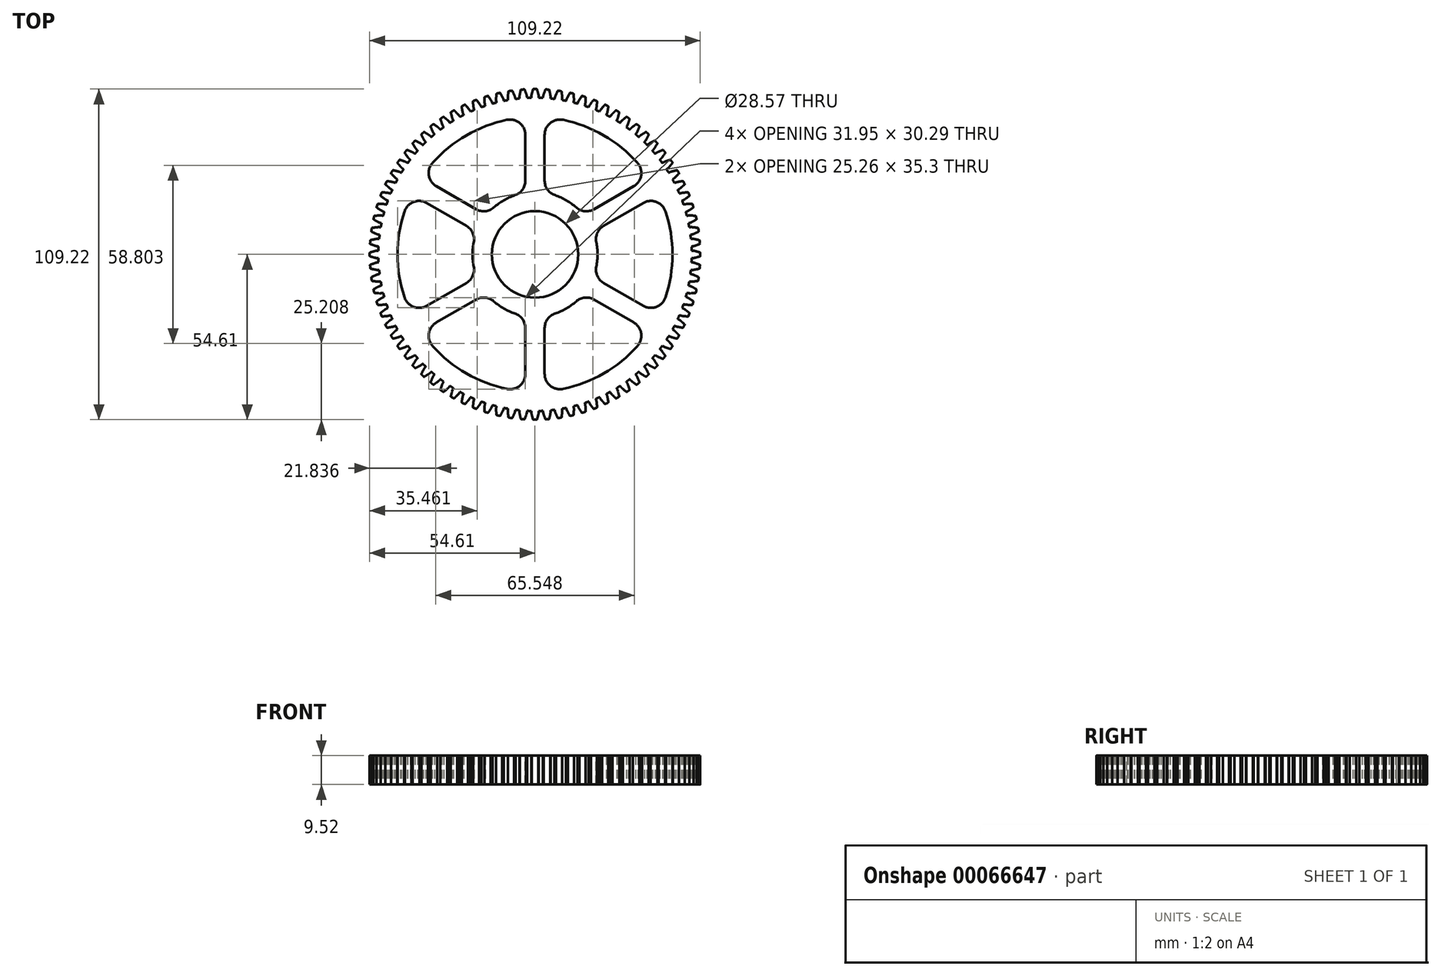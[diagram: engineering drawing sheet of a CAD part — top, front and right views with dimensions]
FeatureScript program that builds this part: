
annotation { "Feature Type Name" : "Feature", "Feature Type Description" : "" }
export const myFeature = defineFeature(function(context is Context, id is Id, definition is map)
    precondition{}
    {
        {
            var Q0;
            Q0=qCreatedBy(makeId("Top.planeOp"),FACE);
            var sketch = newSketch(context, id + "F0", { "sketchPlane" : qUnion([Q0])});
            skArc(sketch, "E0", {"start": v(1.25, 51.74) * mm, "mid": v(0, 51.75) * mm, "end": v(-1.25, 51.74) * mm});
            skArc(sketch, "E1", {"start": v(-1.25, -51.74) * mm, "mid": v(51.74, -1.25) * mm, "end": v(1.25, 51.74) * mm});
            skArc(sketch, "E2", {"start": v(-1.05, 53.12) * mm, "mid": v(-1.2, 52.43) * mm, "end": v(-1.25, 51.74) * mm});
            skArc(sketch, "E3", {"start": v(-0.67, 54.46) * mm, "mid": v(-0.86, 53.79) * mm, "end": v(-1.05, 53.12) * mm});
            skArc(sketch, "E4", {"start": v(-0.48, 54.6) * mm, "mid": v(-0.6, 54.57) * mm, "end": v(-0.67, 54.46) * mm});
            skArc(sketch, "E5", {"start": v(1.25, 51.74) * mm, "mid": v(1.2, 52.43) * mm, "end": v(1.05, 53.12) * mm});
            skArc(sketch, "E6", {"start": v(1.05, 53.12) * mm, "mid": v(0.86, 53.79) * mm, "end": v(0.67, 54.46) * mm});
            skArc(sketch, "E7", {"start": v(0.48, 54.6) * mm, "mid": v(0, 54.61) * mm, "end": v(-0.48, 54.6) * mm});
            skArc(sketch, "E8", {"start": v(0.67, 54.46) * mm, "mid": v(0.6, 54.57) * mm, "end": v(0.48, 54.6) * mm});
            skArc(sketch, "E9", {"start": v(-1.25, 51.74) * mm, "mid": v(-51.75, 0) * mm, "end": v(-1.25, -51.74) * mm});
            skSolve(sketch);
        }
        {
            var Q0;
            Q0=makeQuery(id+"F0.imprint","IMPRINT",FACE,{"disambiguationData":[TD([[makeQuery(id+"F0.imprint","IMPRINT",EDGE,{"derivedFrom":sQuery(id+"F0.wireOp",EDGE,"E0")}),1.0]])]});
            extrude(context, id + "F1", {"entities" : qUnion([Q0]), "endBound" : BoundingType.SYMMETRIC, "depth" : 9.52 * mm});
        }
        {
            var Q0;
            {var subQ0=sQuery(id+"F0.wireOp",EDGE,"E0");Q0=makeQuery(id+"F0.imprint","IMPRINT",FACE,{"disambiguationData":[TD([[makeQuery(id+"F0.imprint","IMPRINT",EDGE,{"derivedFrom":subQ0}),-1.0]])]});}
            var Q1;
            Q1=makeQuery(id+"F1.opExtrude","CAP_FACE",FACE,{"disambiguationData":[OSD([sQuery(id+"F0.wireOp",EDGE,"E0"),sQuery(id+"F0.wireOp",EDGE,"E1"),sQuery(id+"F0.wireOp",EDGE,"E9")])],"isStart":false});
            var Q2;
            Q2=makeQuery(id+"F1.opExtrude","CAP_FACE",FACE,{"disambiguationData":[OSD([sQuery(id+"F0.wireOp",EDGE,"E0"),sQuery(id+"F0.wireOp",EDGE,"E1"),sQuery(id+"F0.wireOp",EDGE,"E9")])],"isStart":true});
            extrude(context, id + "F2", {"entities" : qUnion([Q0]), "endBound" : BoundingType.UP_TO_SURFACE, "endBoundEntityFace" : qUnion([Q1]), "depth" : 25.4 * mm, "hasSecondDirection" : true, "secondDirectionBound" : SecondDirectionBoundingType.UP_TO_SURFACE, "secondDirectionOppositeDirection" : true, "secondDirectionBoundEntityFace" : qUnion([Q2]), "secondDirectionDepth" : 25.4 * mm});
        }
        {
            var Q0;
            Q0=makeQuery(id+"F2.opExtrude","SWEPT_BODY",BODY,{"disambiguationData":[OSD([sQuery(id+"F0.wireOp",EDGE,"E0"),sQuery(id+"F0.wireOp",EDGE,"E2"),sQuery(id+"F0.wireOp",EDGE,"E3"),sQuery(id+"F0.wireOp",EDGE,"E4"),sQuery(id+"F0.wireOp",EDGE,"E5"),sQuery(id+"F0.wireOp",EDGE,"E6"),sQuery(id+"F0.wireOp",EDGE,"E7"),sQuery(id+"F0.wireOp",EDGE,"E8")])]});
            var Q1;
            Q1=makeQuery(id+"F1.opExtrude","SWEPT_FACE",FACE,{"disambiguationData":[OSD([sQuery(id+"F0.wireOp",EDGE,"E0"),sQuery(id+"F0.wireOp",EDGE,"E1"),sQuery(id+"F0.wireOp",EDGE,"E9")])]});
            circularPattern(context, id + "F3", {"operationType" : NewBodyOperationType.ADD, "entities" : qUnion([Q0]), "axis" : qUnion([Q1]), "angle" : 360 * degree, "instanceCount" : 84, "equalSpace" : true});
        }
        {
            var Q0;
            {var subQ0=sQuery(id+"F0.wireOp",EDGE,"E0");var subQ1=makeQuery(id+"F2.opExtrude","CAP_FACE",FACE,{"disambiguationData":[OSD([subQ0,sQuery(id+"F0.wireOp",EDGE,"E2"),sQuery(id+"F0.wireOp",EDGE,"E3"),sQuery(id+"F0.wireOp",EDGE,"E4"),sQuery(id+"F0.wireOp",EDGE,"E5"),sQuery(id+"F0.wireOp",EDGE,"E6"),sQuery(id+"F0.wireOp",EDGE,"E7"),sQuery(id+"F0.wireOp",EDGE,"E8")])],"isStart":false});Q0=makeQuery(id+"F3.boolean.opBoolean","MERGE",FACE,{"derivedFrom":[makeQuery(id+"F1.opExtrude","CAP_FACE",FACE,{"disambiguationData":[OSD([subQ0,sQuery(id+"F0.wireOp",EDGE,"E1"),sQuery(id+"F0.wireOp",EDGE,"E9")])],"isStart":false}),subQ1,makeQuery(id+"F3.opPattern","COPY",FACE,{"derivedFrom":subQ1,"instanceName":"1"}),makeQuery(id+"F3.opPattern","COPY",FACE,{"derivedFrom":subQ1,"instanceName":"2"}),makeQuery(id+"F3.opPattern","COPY",FACE,{"derivedFrom":subQ1,"instanceName":"3"}),makeQuery(id+"F3.opPattern","COPY",FACE,{"derivedFrom":subQ1,"instanceName":"4"}),makeQuery(id+"F3.opPattern","COPY",FACE,{"derivedFrom":subQ1,"instanceName":"5"}),makeQuery(id+"F3.opPattern","COPY",FACE,{"derivedFrom":subQ1,"instanceName":"6"}),makeQuery(id+"F3.opPattern","COPY",FACE,{"derivedFrom":subQ1,"instanceName":"7"}),makeQuery(id+"F3.opPattern","COPY",FACE,{"derivedFrom":subQ1,"instanceName":"8"}),makeQuery(id+"F3.opPattern","COPY",FACE,{"derivedFrom":subQ1,"instanceName":"9"}),makeQuery(id+"F3.opPattern","COPY",FACE,{"derivedFrom":subQ1,"instanceName":"10"}),makeQuery(id+"F3.opPattern","COPY",FACE,{"derivedFrom":subQ1,"instanceName":"11"}),makeQuery(id+"F3.opPattern","COPY",FACE,{"derivedFrom":subQ1,"instanceName":"12"}),makeQuery(id+"F3.opPattern","COPY",FACE,{"derivedFrom":subQ1,"instanceName":"13"}),makeQuery(id+"F3.opPattern","COPY",FACE,{"derivedFrom":subQ1,"instanceName":"14"}),makeQuery(id+"F3.opPattern","COPY",FACE,{"derivedFrom":subQ1,"instanceName":"15"}),makeQuery(id+"F3.opPattern","COPY",FACE,{"derivedFrom":subQ1,"instanceName":"16"}),makeQuery(id+"F3.opPattern","COPY",FACE,{"derivedFrom":subQ1,"instanceName":"17"}),makeQuery(id+"F3.opPattern","COPY",FACE,{"derivedFrom":subQ1,"instanceName":"18"}),makeQuery(id+"F3.opPattern","COPY",FACE,{"derivedFrom":subQ1,"instanceName":"19"}),makeQuery(id+"F3.opPattern","COPY",FACE,{"derivedFrom":subQ1,"instanceName":"20"}),makeQuery(id+"F3.opPattern","COPY",FACE,{"derivedFrom":subQ1,"instanceName":"21"}),makeQuery(id+"F3.opPattern","COPY",FACE,{"derivedFrom":subQ1,"instanceName":"22"}),makeQuery(id+"F3.opPattern","COPY",FACE,{"derivedFrom":subQ1,"instanceName":"23"}),makeQuery(id+"F3.opPattern","COPY",FACE,{"derivedFrom":subQ1,"instanceName":"24"}),makeQuery(id+"F3.opPattern","COPY",FACE,{"derivedFrom":subQ1,"instanceName":"25"}),makeQuery(id+"F3.opPattern","COPY",FACE,{"derivedFrom":subQ1,"instanceName":"26"}),makeQuery(id+"F3.opPattern","COPY",FACE,{"derivedFrom":subQ1,"instanceName":"27"}),makeQuery(id+"F3.opPattern","COPY",FACE,{"derivedFrom":subQ1,"instanceName":"28"}),makeQuery(id+"F3.opPattern","COPY",FACE,{"derivedFrom":subQ1,"instanceName":"29"}),makeQuery(id+"F3.opPattern","COPY",FACE,{"derivedFrom":subQ1,"instanceName":"30"}),makeQuery(id+"F3.opPattern","COPY",FACE,{"derivedFrom":subQ1,"instanceName":"31"}),makeQuery(id+"F3.opPattern","COPY",FACE,{"derivedFrom":subQ1,"instanceName":"32"}),makeQuery(id+"F3.opPattern","COPY",FACE,{"derivedFrom":subQ1,"instanceName":"33"}),makeQuery(id+"F3.opPattern","COPY",FACE,{"derivedFrom":subQ1,"instanceName":"34"}),makeQuery(id+"F3.opPattern","COPY",FACE,{"derivedFrom":subQ1,"instanceName":"35"}),makeQuery(id+"F3.opPattern","COPY",FACE,{"derivedFrom":subQ1,"instanceName":"36"}),makeQuery(id+"F3.opPattern","COPY",FACE,{"derivedFrom":subQ1,"instanceName":"37"}),makeQuery(id+"F3.opPattern","COPY",FACE,{"derivedFrom":subQ1,"instanceName":"38"}),makeQuery(id+"F3.opPattern","COPY",FACE,{"derivedFrom":subQ1,"instanceName":"39"}),makeQuery(id+"F3.opPattern","COPY",FACE,{"derivedFrom":subQ1,"instanceName":"40"}),makeQuery(id+"F3.opPattern","COPY",FACE,{"derivedFrom":subQ1,"instanceName":"41"}),makeQuery(id+"F3.opPattern","COPY",FACE,{"derivedFrom":subQ1,"instanceName":"42"}),makeQuery(id+"F3.opPattern","COPY",FACE,{"derivedFrom":subQ1,"instanceName":"43"}),makeQuery(id+"F3.opPattern","COPY",FACE,{"derivedFrom":subQ1,"instanceName":"44"}),makeQuery(id+"F3.opPattern","COPY",FACE,{"derivedFrom":subQ1,"instanceName":"45"}),makeQuery(id+"F3.opPattern","COPY",FACE,{"derivedFrom":subQ1,"instanceName":"46"}),makeQuery(id+"F3.opPattern","COPY",FACE,{"derivedFrom":subQ1,"instanceName":"47"}),makeQuery(id+"F3.opPattern","COPY",FACE,{"derivedFrom":subQ1,"instanceName":"48"}),makeQuery(id+"F3.opPattern","COPY",FACE,{"derivedFrom":subQ1,"instanceName":"49"}),makeQuery(id+"F3.opPattern","COPY",FACE,{"derivedFrom":subQ1,"instanceName":"50"}),makeQuery(id+"F3.opPattern","COPY",FACE,{"derivedFrom":subQ1,"instanceName":"51"}),makeQuery(id+"F3.opPattern","COPY",FACE,{"derivedFrom":subQ1,"instanceName":"52"}),makeQuery(id+"F3.opPattern","COPY",FACE,{"derivedFrom":subQ1,"instanceName":"53"}),makeQuery(id+"F3.opPattern","COPY",FACE,{"derivedFrom":subQ1,"instanceName":"54"}),makeQuery(id+"F3.opPattern","COPY",FACE,{"derivedFrom":subQ1,"instanceName":"55"}),makeQuery(id+"F3.opPattern","COPY",FACE,{"derivedFrom":subQ1,"instanceName":"56"}),makeQuery(id+"F3.opPattern","COPY",FACE,{"derivedFrom":subQ1,"instanceName":"57"}),makeQuery(id+"F3.opPattern","COPY",FACE,{"derivedFrom":subQ1,"instanceName":"58"}),makeQuery(id+"F3.opPattern","COPY",FACE,{"derivedFrom":subQ1,"instanceName":"59"}),makeQuery(id+"F3.opPattern","COPY",FACE,{"derivedFrom":subQ1,"instanceName":"60"}),makeQuery(id+"F3.opPattern","COPY",FACE,{"derivedFrom":subQ1,"instanceName":"61"}),makeQuery(id+"F3.opPattern","COPY",FACE,{"derivedFrom":subQ1,"instanceName":"62"}),makeQuery(id+"F3.opPattern","COPY",FACE,{"derivedFrom":subQ1,"instanceName":"63"}),makeQuery(id+"F3.opPattern","COPY",FACE,{"derivedFrom":subQ1,"instanceName":"64"}),makeQuery(id+"F3.opPattern","COPY",FACE,{"derivedFrom":subQ1,"instanceName":"65"}),makeQuery(id+"F3.opPattern","COPY",FACE,{"derivedFrom":subQ1,"instanceName":"66"}),makeQuery(id+"F3.opPattern","COPY",FACE,{"derivedFrom":subQ1,"instanceName":"67"}),makeQuery(id+"F3.opPattern","COPY",FACE,{"derivedFrom":subQ1,"instanceName":"68"}),makeQuery(id+"F3.opPattern","COPY",FACE,{"derivedFrom":subQ1,"instanceName":"69"}),makeQuery(id+"F3.opPattern","COPY",FACE,{"derivedFrom":subQ1,"instanceName":"70"}),makeQuery(id+"F3.opPattern","COPY",FACE,{"derivedFrom":subQ1,"instanceName":"71"}),makeQuery(id+"F3.opPattern","COPY",FACE,{"derivedFrom":subQ1,"instanceName":"72"}),makeQuery(id+"F3.opPattern","COPY",FACE,{"derivedFrom":subQ1,"instanceName":"73"}),makeQuery(id+"F3.opPattern","COPY",FACE,{"derivedFrom":subQ1,"instanceName":"74"}),makeQuery(id+"F3.opPattern","COPY",FACE,{"derivedFrom":subQ1,"instanceName":"75"}),makeQuery(id+"F3.opPattern","COPY",FACE,{"derivedFrom":subQ1,"instanceName":"76"}),makeQuery(id+"F3.opPattern","COPY",FACE,{"derivedFrom":subQ1,"instanceName":"77"}),makeQuery(id+"F3.opPattern","COPY",FACE,{"derivedFrom":subQ1,"instanceName":"78"}),makeQuery(id+"F3.opPattern","COPY",FACE,{"derivedFrom":subQ1,"instanceName":"79"}),makeQuery(id+"F3.opPattern","COPY",FACE,{"derivedFrom":subQ1,"instanceName":"80"}),makeQuery(id+"F3.opPattern","COPY",FACE,{"derivedFrom":subQ1,"instanceName":"81"}),makeQuery(id+"F3.opPattern","COPY",FACE,{"derivedFrom":subQ1,"instanceName":"82"}),makeQuery(id+"F3.opPattern","COPY",FACE,{"derivedFrom":subQ1,"instanceName":"83"})]});}
            var sketch = newSketch(context, id + "F4", { "sketchPlane" : qUnion([Q0])});
            skCircle(sketch, "E10", {"center": v(0, 0) * mm, "radius": 14.29 * mm});
            skSolve(sketch);
        }
        {
            var Q0;
            Q0=makeQuery(id+"F4.imprint","IMPRINT",FACE,{"disambiguationData":[TD([[makeQuery(id+"F4.imprint","IMPRINT",EDGE,{"derivedFrom":sQuery(id+"F4.wireOp",EDGE,"E10")}),1.0]])]});
            extrude(context, id + "F5", {"entities" : qUnion([Q0]), "operationType" : NewBodyOperationType.REMOVE, "endBound" : BoundingType.UP_TO_NEXT, "oppositeDirection" : true, "depth" : 25.4 * mm});
        }
        {
            var Q0;
            {var subQ0=sQuery(id+"F0.wireOp",EDGE,"E0");var subQ1=makeQuery(id+"F2.opExtrude","CAP_FACE",FACE,{"disambiguationData":[OSD([subQ0,sQuery(id+"F0.wireOp",EDGE,"E2"),sQuery(id+"F0.wireOp",EDGE,"E3"),sQuery(id+"F0.wireOp",EDGE,"E4"),sQuery(id+"F0.wireOp",EDGE,"E5"),sQuery(id+"F0.wireOp",EDGE,"E6"),sQuery(id+"F0.wireOp",EDGE,"E7"),sQuery(id+"F0.wireOp",EDGE,"E8")])],"isStart":false});Q0=makeQuery(id+"F3.boolean.opBoolean","MERGE",FACE,{"derivedFrom":[makeQuery(id+"F1.opExtrude","CAP_FACE",FACE,{"disambiguationData":[OSD([subQ0,sQuery(id+"F0.wireOp",EDGE,"E1"),sQuery(id+"F0.wireOp",EDGE,"E9")])],"isStart":false}),subQ1,makeQuery(id+"F3.opPattern","COPY",FACE,{"derivedFrom":subQ1,"instanceName":"1"}),makeQuery(id+"F3.opPattern","COPY",FACE,{"derivedFrom":subQ1,"instanceName":"2"}),makeQuery(id+"F3.opPattern","COPY",FACE,{"derivedFrom":subQ1,"instanceName":"3"}),makeQuery(id+"F3.opPattern","COPY",FACE,{"derivedFrom":subQ1,"instanceName":"4"}),makeQuery(id+"F3.opPattern","COPY",FACE,{"derivedFrom":subQ1,"instanceName":"5"}),makeQuery(id+"F3.opPattern","COPY",FACE,{"derivedFrom":subQ1,"instanceName":"6"}),makeQuery(id+"F3.opPattern","COPY",FACE,{"derivedFrom":subQ1,"instanceName":"7"}),makeQuery(id+"F3.opPattern","COPY",FACE,{"derivedFrom":subQ1,"instanceName":"8"}),makeQuery(id+"F3.opPattern","COPY",FACE,{"derivedFrom":subQ1,"instanceName":"9"}),makeQuery(id+"F3.opPattern","COPY",FACE,{"derivedFrom":subQ1,"instanceName":"10"}),makeQuery(id+"F3.opPattern","COPY",FACE,{"derivedFrom":subQ1,"instanceName":"11"}),makeQuery(id+"F3.opPattern","COPY",FACE,{"derivedFrom":subQ1,"instanceName":"12"}),makeQuery(id+"F3.opPattern","COPY",FACE,{"derivedFrom":subQ1,"instanceName":"13"}),makeQuery(id+"F3.opPattern","COPY",FACE,{"derivedFrom":subQ1,"instanceName":"14"}),makeQuery(id+"F3.opPattern","COPY",FACE,{"derivedFrom":subQ1,"instanceName":"15"}),makeQuery(id+"F3.opPattern","COPY",FACE,{"derivedFrom":subQ1,"instanceName":"16"}),makeQuery(id+"F3.opPattern","COPY",FACE,{"derivedFrom":subQ1,"instanceName":"17"}),makeQuery(id+"F3.opPattern","COPY",FACE,{"derivedFrom":subQ1,"instanceName":"18"}),makeQuery(id+"F3.opPattern","COPY",FACE,{"derivedFrom":subQ1,"instanceName":"19"}),makeQuery(id+"F3.opPattern","COPY",FACE,{"derivedFrom":subQ1,"instanceName":"20"}),makeQuery(id+"F3.opPattern","COPY",FACE,{"derivedFrom":subQ1,"instanceName":"21"}),makeQuery(id+"F3.opPattern","COPY",FACE,{"derivedFrom":subQ1,"instanceName":"22"}),makeQuery(id+"F3.opPattern","COPY",FACE,{"derivedFrom":subQ1,"instanceName":"23"}),makeQuery(id+"F3.opPattern","COPY",FACE,{"derivedFrom":subQ1,"instanceName":"24"}),makeQuery(id+"F3.opPattern","COPY",FACE,{"derivedFrom":subQ1,"instanceName":"25"}),makeQuery(id+"F3.opPattern","COPY",FACE,{"derivedFrom":subQ1,"instanceName":"26"}),makeQuery(id+"F3.opPattern","COPY",FACE,{"derivedFrom":subQ1,"instanceName":"27"}),makeQuery(id+"F3.opPattern","COPY",FACE,{"derivedFrom":subQ1,"instanceName":"28"}),makeQuery(id+"F3.opPattern","COPY",FACE,{"derivedFrom":subQ1,"instanceName":"29"}),makeQuery(id+"F3.opPattern","COPY",FACE,{"derivedFrom":subQ1,"instanceName":"30"}),makeQuery(id+"F3.opPattern","COPY",FACE,{"derivedFrom":subQ1,"instanceName":"31"}),makeQuery(id+"F3.opPattern","COPY",FACE,{"derivedFrom":subQ1,"instanceName":"32"}),makeQuery(id+"F3.opPattern","COPY",FACE,{"derivedFrom":subQ1,"instanceName":"33"}),makeQuery(id+"F3.opPattern","COPY",FACE,{"derivedFrom":subQ1,"instanceName":"34"}),makeQuery(id+"F3.opPattern","COPY",FACE,{"derivedFrom":subQ1,"instanceName":"35"}),makeQuery(id+"F3.opPattern","COPY",FACE,{"derivedFrom":subQ1,"instanceName":"36"}),makeQuery(id+"F3.opPattern","COPY",FACE,{"derivedFrom":subQ1,"instanceName":"37"}),makeQuery(id+"F3.opPattern","COPY",FACE,{"derivedFrom":subQ1,"instanceName":"38"}),makeQuery(id+"F3.opPattern","COPY",FACE,{"derivedFrom":subQ1,"instanceName":"39"}),makeQuery(id+"F3.opPattern","COPY",FACE,{"derivedFrom":subQ1,"instanceName":"40"}),makeQuery(id+"F3.opPattern","COPY",FACE,{"derivedFrom":subQ1,"instanceName":"41"}),makeQuery(id+"F3.opPattern","COPY",FACE,{"derivedFrom":subQ1,"instanceName":"42"}),makeQuery(id+"F3.opPattern","COPY",FACE,{"derivedFrom":subQ1,"instanceName":"43"}),makeQuery(id+"F3.opPattern","COPY",FACE,{"derivedFrom":subQ1,"instanceName":"44"}),makeQuery(id+"F3.opPattern","COPY",FACE,{"derivedFrom":subQ1,"instanceName":"45"}),makeQuery(id+"F3.opPattern","COPY",FACE,{"derivedFrom":subQ1,"instanceName":"46"}),makeQuery(id+"F3.opPattern","COPY",FACE,{"derivedFrom":subQ1,"instanceName":"47"}),makeQuery(id+"F3.opPattern","COPY",FACE,{"derivedFrom":subQ1,"instanceName":"48"}),makeQuery(id+"F3.opPattern","COPY",FACE,{"derivedFrom":subQ1,"instanceName":"49"}),makeQuery(id+"F3.opPattern","COPY",FACE,{"derivedFrom":subQ1,"instanceName":"50"}),makeQuery(id+"F3.opPattern","COPY",FACE,{"derivedFrom":subQ1,"instanceName":"51"}),makeQuery(id+"F3.opPattern","COPY",FACE,{"derivedFrom":subQ1,"instanceName":"52"}),makeQuery(id+"F3.opPattern","COPY",FACE,{"derivedFrom":subQ1,"instanceName":"53"}),makeQuery(id+"F3.opPattern","COPY",FACE,{"derivedFrom":subQ1,"instanceName":"54"}),makeQuery(id+"F3.opPattern","COPY",FACE,{"derivedFrom":subQ1,"instanceName":"55"}),makeQuery(id+"F3.opPattern","COPY",FACE,{"derivedFrom":subQ1,"instanceName":"56"}),makeQuery(id+"F3.opPattern","COPY",FACE,{"derivedFrom":subQ1,"instanceName":"57"}),makeQuery(id+"F3.opPattern","COPY",FACE,{"derivedFrom":subQ1,"instanceName":"58"}),makeQuery(id+"F3.opPattern","COPY",FACE,{"derivedFrom":subQ1,"instanceName":"59"}),makeQuery(id+"F3.opPattern","COPY",FACE,{"derivedFrom":subQ1,"instanceName":"60"}),makeQuery(id+"F3.opPattern","COPY",FACE,{"derivedFrom":subQ1,"instanceName":"61"}),makeQuery(id+"F3.opPattern","COPY",FACE,{"derivedFrom":subQ1,"instanceName":"62"}),makeQuery(id+"F3.opPattern","COPY",FACE,{"derivedFrom":subQ1,"instanceName":"63"}),makeQuery(id+"F3.opPattern","COPY",FACE,{"derivedFrom":subQ1,"instanceName":"64"}),makeQuery(id+"F3.opPattern","COPY",FACE,{"derivedFrom":subQ1,"instanceName":"65"}),makeQuery(id+"F3.opPattern","COPY",FACE,{"derivedFrom":subQ1,"instanceName":"66"}),makeQuery(id+"F3.opPattern","COPY",FACE,{"derivedFrom":subQ1,"instanceName":"67"}),makeQuery(id+"F3.opPattern","COPY",FACE,{"derivedFrom":subQ1,"instanceName":"68"}),makeQuery(id+"F3.opPattern","COPY",FACE,{"derivedFrom":subQ1,"instanceName":"69"}),makeQuery(id+"F3.opPattern","COPY",FACE,{"derivedFrom":subQ1,"instanceName":"70"}),makeQuery(id+"F3.opPattern","COPY",FACE,{"derivedFrom":subQ1,"instanceName":"71"}),makeQuery(id+"F3.opPattern","COPY",FACE,{"derivedFrom":subQ1,"instanceName":"72"}),makeQuery(id+"F3.opPattern","COPY",FACE,{"derivedFrom":subQ1,"instanceName":"73"}),makeQuery(id+"F3.opPattern","COPY",FACE,{"derivedFrom":subQ1,"instanceName":"74"}),makeQuery(id+"F3.opPattern","COPY",FACE,{"derivedFrom":subQ1,"instanceName":"75"}),makeQuery(id+"F3.opPattern","COPY",FACE,{"derivedFrom":subQ1,"instanceName":"76"}),makeQuery(id+"F3.opPattern","COPY",FACE,{"derivedFrom":subQ1,"instanceName":"77"}),makeQuery(id+"F3.opPattern","COPY",FACE,{"derivedFrom":subQ1,"instanceName":"78"}),makeQuery(id+"F3.opPattern","COPY",FACE,{"derivedFrom":subQ1,"instanceName":"79"}),makeQuery(id+"F3.opPattern","COPY",FACE,{"derivedFrom":subQ1,"instanceName":"80"}),makeQuery(id+"F3.opPattern","COPY",FACE,{"derivedFrom":subQ1,"instanceName":"81"}),makeQuery(id+"F3.opPattern","COPY",FACE,{"derivedFrom":subQ1,"instanceName":"82"}),makeQuery(id+"F3.opPattern","COPY",FACE,{"derivedFrom":subQ1,"instanceName":"83"})]});}
            var sketch = newSketch(context, id + "F6", { "sketchPlane" : qUnion([Q0])});
            skArc(sketch, "E11", {"start": v(0, 20.64) * mm, "mid": v(-10.32, 17.87) * mm, "end": v(-17.87, 10.32) * mm});
            skArc(sketch, "E12", {"start": v(0, 45.4) * mm, "mid": v(-22.7, 39.32) * mm, "end": v(-39.32, 22.7) * mm});
            skLineSegment(sketch, "E13", {"start": v(0, 20.64) * mm, "end": v(0, 45.4) * mm, "construction": true});
            skLineSegment(sketch, "E14", {"start": v(-17.87, 10.32) * mm, "end": v(-39.32, 22.7) * mm, "construction": true});
            skLineSegment(sketch, "E15.0", {"start": v(-16.07, 12.95) * mm, "end": v(-37.64, 25.4) * mm});
            skLineSegment(sketch, "E16.0", {"start": v(-3.18, 20.4) * mm, "end": v(-3.18, 45.3) * mm});
            skSolve(sketch);
        }
        {
            var Q0;
            {var subQ0=sQuery(id+"F6.wireOp",EDGE,"E15.0");Q0=makeQuery(id+"F6.imprint","IMPRINT",FACE,{"disambiguationData":[TD([[makeQuery(id+"F6.imprint","IMPRINT",EDGE,{"derivedFrom":subQ0}),-1.0]])]});}
            var Q1;
            {var subQ0=sQuery(id+"F0.wireOp",EDGE,"E0");var subQ1=makeQuery(id+"F2.opExtrude","CAP_FACE",FACE,{"disambiguationData":[OSD([subQ0,sQuery(id+"F0.wireOp",EDGE,"E2"),sQuery(id+"F0.wireOp",EDGE,"E3"),sQuery(id+"F0.wireOp",EDGE,"E4"),sQuery(id+"F0.wireOp",EDGE,"E5"),sQuery(id+"F0.wireOp",EDGE,"E6"),sQuery(id+"F0.wireOp",EDGE,"E7"),sQuery(id+"F0.wireOp",EDGE,"E8")])],"isStart":true});Q1=makeQuery(id+"F3.boolean.opBoolean","MERGE",FACE,{"derivedFrom":[makeQuery(id+"F1.opExtrude","CAP_FACE",FACE,{"disambiguationData":[OSD([subQ0,sQuery(id+"F0.wireOp",EDGE,"E1"),sQuery(id+"F0.wireOp",EDGE,"E9")])],"isStart":true}),subQ1,makeQuery(id+"F3.opPattern","COPY",FACE,{"derivedFrom":subQ1,"instanceName":"1"}),makeQuery(id+"F3.opPattern","COPY",FACE,{"derivedFrom":subQ1,"instanceName":"2"}),makeQuery(id+"F3.opPattern","COPY",FACE,{"derivedFrom":subQ1,"instanceName":"3"}),makeQuery(id+"F3.opPattern","COPY",FACE,{"derivedFrom":subQ1,"instanceName":"4"}),makeQuery(id+"F3.opPattern","COPY",FACE,{"derivedFrom":subQ1,"instanceName":"5"}),makeQuery(id+"F3.opPattern","COPY",FACE,{"derivedFrom":subQ1,"instanceName":"6"}),makeQuery(id+"F3.opPattern","COPY",FACE,{"derivedFrom":subQ1,"instanceName":"7"}),makeQuery(id+"F3.opPattern","COPY",FACE,{"derivedFrom":subQ1,"instanceName":"8"}),makeQuery(id+"F3.opPattern","COPY",FACE,{"derivedFrom":subQ1,"instanceName":"9"}),makeQuery(id+"F3.opPattern","COPY",FACE,{"derivedFrom":subQ1,"instanceName":"10"}),makeQuery(id+"F3.opPattern","COPY",FACE,{"derivedFrom":subQ1,"instanceName":"11"}),makeQuery(id+"F3.opPattern","COPY",FACE,{"derivedFrom":subQ1,"instanceName":"12"}),makeQuery(id+"F3.opPattern","COPY",FACE,{"derivedFrom":subQ1,"instanceName":"13"}),makeQuery(id+"F3.opPattern","COPY",FACE,{"derivedFrom":subQ1,"instanceName":"14"}),makeQuery(id+"F3.opPattern","COPY",FACE,{"derivedFrom":subQ1,"instanceName":"15"}),makeQuery(id+"F3.opPattern","COPY",FACE,{"derivedFrom":subQ1,"instanceName":"16"}),makeQuery(id+"F3.opPattern","COPY",FACE,{"derivedFrom":subQ1,"instanceName":"17"}),makeQuery(id+"F3.opPattern","COPY",FACE,{"derivedFrom":subQ1,"instanceName":"18"}),makeQuery(id+"F3.opPattern","COPY",FACE,{"derivedFrom":subQ1,"instanceName":"19"}),makeQuery(id+"F3.opPattern","COPY",FACE,{"derivedFrom":subQ1,"instanceName":"20"}),makeQuery(id+"F3.opPattern","COPY",FACE,{"derivedFrom":subQ1,"instanceName":"21"}),makeQuery(id+"F3.opPattern","COPY",FACE,{"derivedFrom":subQ1,"instanceName":"22"}),makeQuery(id+"F3.opPattern","COPY",FACE,{"derivedFrom":subQ1,"instanceName":"23"}),makeQuery(id+"F3.opPattern","COPY",FACE,{"derivedFrom":subQ1,"instanceName":"24"}),makeQuery(id+"F3.opPattern","COPY",FACE,{"derivedFrom":subQ1,"instanceName":"25"}),makeQuery(id+"F3.opPattern","COPY",FACE,{"derivedFrom":subQ1,"instanceName":"26"}),makeQuery(id+"F3.opPattern","COPY",FACE,{"derivedFrom":subQ1,"instanceName":"27"}),makeQuery(id+"F3.opPattern","COPY",FACE,{"derivedFrom":subQ1,"instanceName":"28"}),makeQuery(id+"F3.opPattern","COPY",FACE,{"derivedFrom":subQ1,"instanceName":"29"}),makeQuery(id+"F3.opPattern","COPY",FACE,{"derivedFrom":subQ1,"instanceName":"30"}),makeQuery(id+"F3.opPattern","COPY",FACE,{"derivedFrom":subQ1,"instanceName":"31"}),makeQuery(id+"F3.opPattern","COPY",FACE,{"derivedFrom":subQ1,"instanceName":"32"}),makeQuery(id+"F3.opPattern","COPY",FACE,{"derivedFrom":subQ1,"instanceName":"33"}),makeQuery(id+"F3.opPattern","COPY",FACE,{"derivedFrom":subQ1,"instanceName":"34"}),makeQuery(id+"F3.opPattern","COPY",FACE,{"derivedFrom":subQ1,"instanceName":"35"}),makeQuery(id+"F3.opPattern","COPY",FACE,{"derivedFrom":subQ1,"instanceName":"36"}),makeQuery(id+"F3.opPattern","COPY",FACE,{"derivedFrom":subQ1,"instanceName":"37"}),makeQuery(id+"F3.opPattern","COPY",FACE,{"derivedFrom":subQ1,"instanceName":"38"}),makeQuery(id+"F3.opPattern","COPY",FACE,{"derivedFrom":subQ1,"instanceName":"39"}),makeQuery(id+"F3.opPattern","COPY",FACE,{"derivedFrom":subQ1,"instanceName":"40"}),makeQuery(id+"F3.opPattern","COPY",FACE,{"derivedFrom":subQ1,"instanceName":"41"}),makeQuery(id+"F3.opPattern","COPY",FACE,{"derivedFrom":subQ1,"instanceName":"42"}),makeQuery(id+"F3.opPattern","COPY",FACE,{"derivedFrom":subQ1,"instanceName":"43"}),makeQuery(id+"F3.opPattern","COPY",FACE,{"derivedFrom":subQ1,"instanceName":"44"}),makeQuery(id+"F3.opPattern","COPY",FACE,{"derivedFrom":subQ1,"instanceName":"45"}),makeQuery(id+"F3.opPattern","COPY",FACE,{"derivedFrom":subQ1,"instanceName":"46"}),makeQuery(id+"F3.opPattern","COPY",FACE,{"derivedFrom":subQ1,"instanceName":"47"}),makeQuery(id+"F3.opPattern","COPY",FACE,{"derivedFrom":subQ1,"instanceName":"48"}),makeQuery(id+"F3.opPattern","COPY",FACE,{"derivedFrom":subQ1,"instanceName":"49"}),makeQuery(id+"F3.opPattern","COPY",FACE,{"derivedFrom":subQ1,"instanceName":"50"}),makeQuery(id+"F3.opPattern","COPY",FACE,{"derivedFrom":subQ1,"instanceName":"51"}),makeQuery(id+"F3.opPattern","COPY",FACE,{"derivedFrom":subQ1,"instanceName":"52"}),makeQuery(id+"F3.opPattern","COPY",FACE,{"derivedFrom":subQ1,"instanceName":"53"}),makeQuery(id+"F3.opPattern","COPY",FACE,{"derivedFrom":subQ1,"instanceName":"54"}),makeQuery(id+"F3.opPattern","COPY",FACE,{"derivedFrom":subQ1,"instanceName":"55"}),makeQuery(id+"F3.opPattern","COPY",FACE,{"derivedFrom":subQ1,"instanceName":"56"}),makeQuery(id+"F3.opPattern","COPY",FACE,{"derivedFrom":subQ1,"instanceName":"57"}),makeQuery(id+"F3.opPattern","COPY",FACE,{"derivedFrom":subQ1,"instanceName":"58"}),makeQuery(id+"F3.opPattern","COPY",FACE,{"derivedFrom":subQ1,"instanceName":"59"}),makeQuery(id+"F3.opPattern","COPY",FACE,{"derivedFrom":subQ1,"instanceName":"60"}),makeQuery(id+"F3.opPattern","COPY",FACE,{"derivedFrom":subQ1,"instanceName":"61"}),makeQuery(id+"F3.opPattern","COPY",FACE,{"derivedFrom":subQ1,"instanceName":"62"}),makeQuery(id+"F3.opPattern","COPY",FACE,{"derivedFrom":subQ1,"instanceName":"63"}),makeQuery(id+"F3.opPattern","COPY",FACE,{"derivedFrom":subQ1,"instanceName":"64"}),makeQuery(id+"F3.opPattern","COPY",FACE,{"derivedFrom":subQ1,"instanceName":"65"}),makeQuery(id+"F3.opPattern","COPY",FACE,{"derivedFrom":subQ1,"instanceName":"66"}),makeQuery(id+"F3.opPattern","COPY",FACE,{"derivedFrom":subQ1,"instanceName":"67"}),makeQuery(id+"F3.opPattern","COPY",FACE,{"derivedFrom":subQ1,"instanceName":"68"}),makeQuery(id+"F3.opPattern","COPY",FACE,{"derivedFrom":subQ1,"instanceName":"69"}),makeQuery(id+"F3.opPattern","COPY",FACE,{"derivedFrom":subQ1,"instanceName":"70"}),makeQuery(id+"F3.opPattern","COPY",FACE,{"derivedFrom":subQ1,"instanceName":"71"}),makeQuery(id+"F3.opPattern","COPY",FACE,{"derivedFrom":subQ1,"instanceName":"72"}),makeQuery(id+"F3.opPattern","COPY",FACE,{"derivedFrom":subQ1,"instanceName":"73"}),makeQuery(id+"F3.opPattern","COPY",FACE,{"derivedFrom":subQ1,"instanceName":"74"}),makeQuery(id+"F3.opPattern","COPY",FACE,{"derivedFrom":subQ1,"instanceName":"75"}),makeQuery(id+"F3.opPattern","COPY",FACE,{"derivedFrom":subQ1,"instanceName":"76"}),makeQuery(id+"F3.opPattern","COPY",FACE,{"derivedFrom":subQ1,"instanceName":"77"}),makeQuery(id+"F3.opPattern","COPY",FACE,{"derivedFrom":subQ1,"instanceName":"78"}),makeQuery(id+"F3.opPattern","COPY",FACE,{"derivedFrom":subQ1,"instanceName":"79"}),makeQuery(id+"F3.opPattern","COPY",FACE,{"derivedFrom":subQ1,"instanceName":"80"}),makeQuery(id+"F3.opPattern","COPY",FACE,{"derivedFrom":subQ1,"instanceName":"81"}),makeQuery(id+"F3.opPattern","COPY",FACE,{"derivedFrom":subQ1,"instanceName":"82"}),makeQuery(id+"F3.opPattern","COPY",FACE,{"derivedFrom":subQ1,"instanceName":"83"})]});}
            extrude(context, id + "F7", {"entities" : qUnion([Q0]), "endBound" : BoundingType.UP_TO_SURFACE, "oppositeDirection" : true, "endBoundEntityFace" : qUnion([Q1]), "depth" : 25.4 * mm});
        }
        {
            var Q0;
            Q0=makeQuery(id+"F7.opExtrude","SWEPT_EDGE",EDGE,{"disambiguationData":[OSD([sQuery(id+"F6.wireOp",EDGE,"E12"),sQuery(id+"F6.wireOp",EDGE,"E16.0")])]});
            var Q1;
            Q1=makeQuery(id+"F7.opExtrude","SWEPT_EDGE",EDGE,{"disambiguationData":[OSD([sQuery(id+"F6.wireOp",EDGE,"E11"),sQuery(id+"F6.wireOp",EDGE,"E16.0")])]});
            var Q2;
            Q2=makeQuery(id+"F7.opExtrude","SWEPT_EDGE",EDGE,{"disambiguationData":[OSD([sQuery(id+"F6.wireOp",EDGE,"E11"),sQuery(id+"F6.wireOp",EDGE,"E15.0")])]});
            var Q3;
            Q3=makeQuery(id+"F7.opExtrude","SWEPT_EDGE",EDGE,{"disambiguationData":[OSD([sQuery(id+"F6.wireOp",EDGE,"E12"),sQuery(id+"F6.wireOp",EDGE,"E15.0")])]});
            fillet(context, id + "F8", {"entities" : qUnion([Q0, Q1, Q2, Q3]), "radius" : 5.08 * mm, "tangentPropagation" : true, "allowEdgeOverflow" : false});
        }
        {
            var Q0;
            Q0=makeQuery(id+"F7.opExtrude","SWEPT_BODY",BODY,{"disambiguationData":[OSD([sQuery(id+"F6.wireOp",EDGE,"E11"),sQuery(id+"F6.wireOp",EDGE,"E12"),sQuery(id+"F6.wireOp",EDGE,"E15.0"),sQuery(id+"F6.wireOp",EDGE,"E16.0")])]});
            var Q1;
            Q1=makeQuery(id+"F5.boolean.opBoolean","COPY",FACE,{"derivedFrom":makeQuery(id+"F5.opExtrude","SWEPT_FACE",FACE,{"disambiguationData":[OSD([sQuery(id+"F4.wireOp",EDGE,"E10")])]})});
            circularPattern(context, id + "F9", {"operationType" : NewBodyOperationType.REMOVE, "entities" : qUnion([Q0]), "axis" : qUnion([Q1]), "angle" : 360 * degree, "instanceCount" : 6, "equalSpace" : true});
        }
    });
